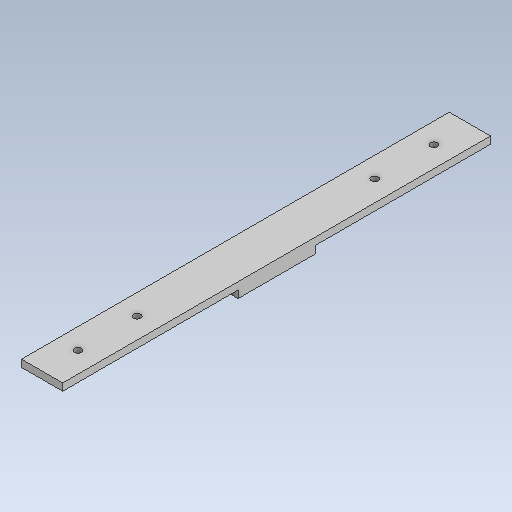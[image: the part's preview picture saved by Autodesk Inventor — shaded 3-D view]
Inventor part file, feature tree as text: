
AUTODESK INVENTOR PART (.ipt)
format: ipt  version: 2021 (Build 250183000, 183)  size: 128,000 bytes
history: native  units: mm
features: extrude x5, sketch x5, reference x4, other x4, projected_geometry x2
ambient origin geometry x8: Origin, YZ Plane, XZ Plane, XY Plane, X Axis, Y Axis, Z Axis, Center Point
bodies: Solid1 (feature_tree)
feature tree (20):
  extrude  "Extrusion1"  Depth=4.0mm TaperAngle=0.0deg
  extrude  "Extrusion2"  Depth=35.0mm
  extrude  "Extrusion3"  TaperAngle=0.0deg  [1 undecoded]
  extrude  "Extrusion4"  Depth=4.0mm TaperAngle=0.0deg
  extrude  "Extrusion5"  [1 undecoded]
  sketch  "Sketch1"  dims[d2=238.782mm d3=4.0mm d4=0.0mm]
  sketch  "Sketch3"  dims[d5=17.5mm d6=35.0mm]
  sketch  "Sketch4"  dims[d7=4.15mm d8=0.0mm d9=0.0mm d10=0.0mm]
  reference  "Reference1"
  reference  "Reference2"
  reference  "Reference3"
  reference  "Reference4"
  sketch  "Sketch5"  dims[d11=4.0mm d12=0.0mm d13=4.0mm d14=0.0mm]
  projected_geometry  "Projected Loop1"
  sketch  "Sketch6"
  projected_geometry  "Projected Loop2"
  parser-record x1  (decoder bookkeeping rows leaked as tree rows — omitted from the tree; the rows remain in map.json)
  other  "assembly.iam"
  other  "battery_box:1"
  other  "battery_box:2"
note: 2 required parameter values undecoded (feature->parameter linkage not recoverable at this tier; creation-order binding heuristic only, values carry confidence <= 0.55)
note: 1 file-system path scrubbed to <path> (originals preserved in map.json)
